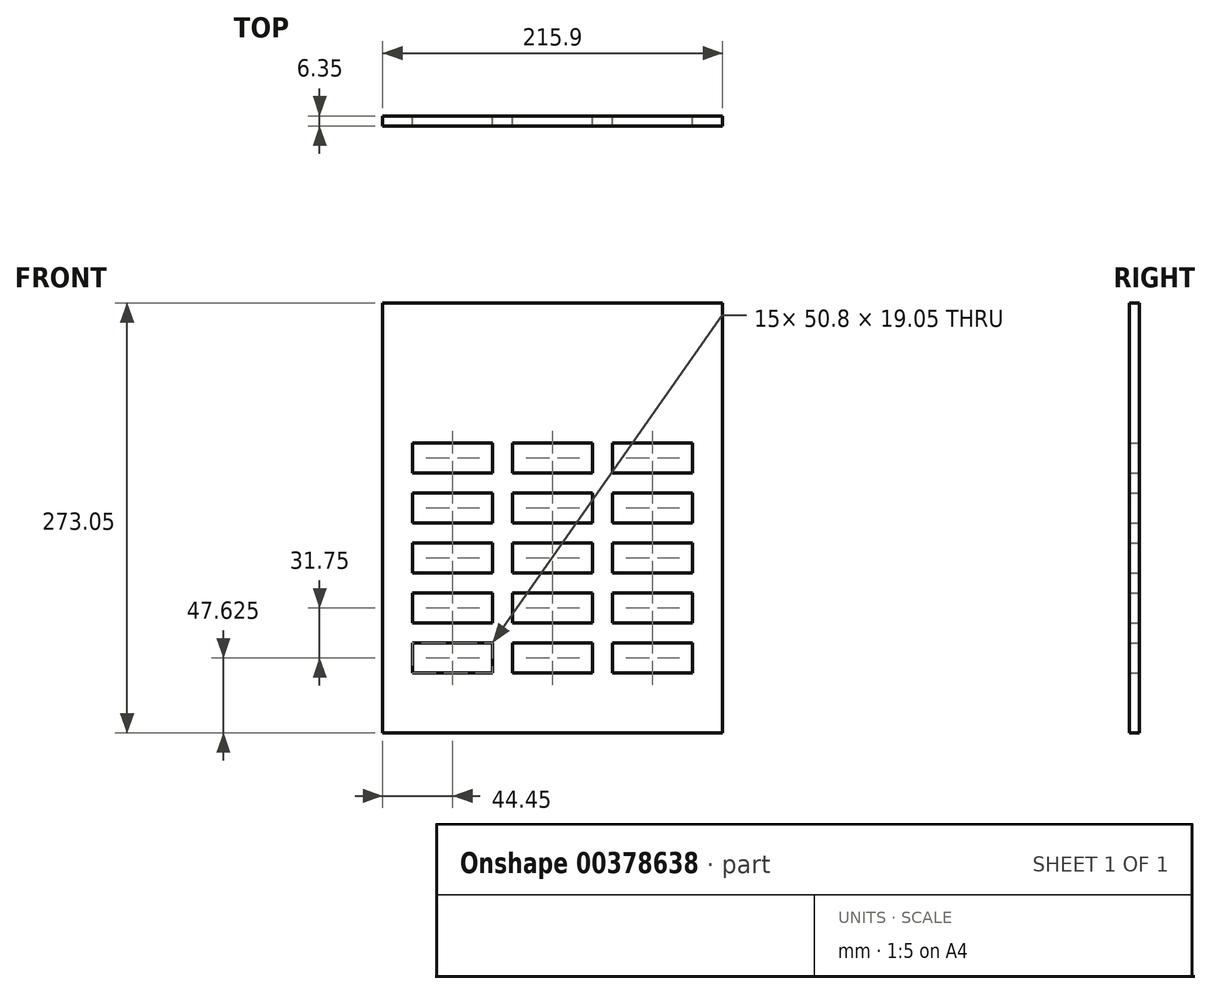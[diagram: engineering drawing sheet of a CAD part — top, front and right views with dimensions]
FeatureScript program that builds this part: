
annotation { "Feature Type Name" : "Feature", "Feature Type Description" : "" }
export const myFeature = defineFeature(function(context is Context, id is Id, definition is map)
    precondition{}
    {
        {
            var Q0;
            Q0=qCreatedBy(makeId("Front.planeOp"),FACE);
            var sketch = newSketch(context, id + "F0", { "sketchPlane" : qUnion([Q0])});
            skLineSegment(sketch, "E0.bottom", {"start": v(-107.95, 0) * mm, "end": v(107.95, 0) * mm});
            skLineSegment(sketch, "E0.top", {"start": v(-107.95, 273.05) * mm, "end": v(107.95, 273.05) * mm});
            skLineSegment(sketch, "E0.left", {"start": v(-107.95, 0) * mm, "end": v(-107.95, 273.05) * mm});
            skLineSegment(sketch, "E0.right", {"start": v(107.95, 0) * mm, "end": v(107.95, 273.05) * mm});
            skPoint(sketch, "E1", {"position": v(0, 273.05) * mm});
            skLineSegment(sketch, "E2.bottom", {"start": v(-88.9, 184.15) * mm, "end": v(-38.1, 184.15) * mm});
            skLineSegment(sketch, "E2.top", {"start": v(-88.9, 165.1) * mm, "end": v(-38.1, 165.1) * mm});
            skLineSegment(sketch, "E2.left", {"start": v(-88.9, 184.15) * mm, "end": v(-88.9, 165.1) * mm});
            skLineSegment(sketch, "E2.right", {"start": v(-38.1, 184.15) * mm, "end": v(-38.1, 165.1) * mm});
            skLineSegment(sketch, "E3.bottom", {"start": v(-25.4, 184.15) * mm, "end": v(25.4, 184.15) * mm});
            skLineSegment(sketch, "E3.top", {"start": v(-25.4, 165.1) * mm, "end": v(25.4, 165.1) * mm});
            skLineSegment(sketch, "E3.left", {"start": v(-25.4, 184.15) * mm, "end": v(-25.4, 165.1) * mm});
            skLineSegment(sketch, "E3.right", {"start": v(25.4, 184.15) * mm, "end": v(25.4, 165.1) * mm});
            skLineSegment(sketch, "E4.bottom", {"start": v(38.1, 184.15) * mm, "end": v(88.9, 184.15) * mm});
            skLineSegment(sketch, "E4.top", {"start": v(38.1, 165.1) * mm, "end": v(88.9, 165.1) * mm});
            skLineSegment(sketch, "E4.left", {"start": v(38.1, 184.15) * mm, "end": v(38.1, 165.1) * mm});
            skLineSegment(sketch, "E4.right", {"start": v(88.9, 184.15) * mm, "end": v(88.9, 165.1) * mm});
            skLineSegment(sketch, "E5.bottom", {"start": v(-88.9, 152.4) * mm, "end": v(-38.1, 152.4) * mm});
            skLineSegment(sketch, "E5.top", {"start": v(-88.9, 133.35) * mm, "end": v(-38.1, 133.35) * mm});
            skLineSegment(sketch, "E5.left", {"start": v(-88.9, 152.4) * mm, "end": v(-88.9, 133.35) * mm});
            skLineSegment(sketch, "E5.right", {"start": v(-38.1, 152.4) * mm, "end": v(-38.1, 133.35) * mm});
            skLineSegment(sketch, "E6.bottom", {"start": v(-25.4, 152.4) * mm, "end": v(25.4, 152.4) * mm});
            skLineSegment(sketch, "E6.top", {"start": v(-25.4, 133.35) * mm, "end": v(25.4, 133.35) * mm});
            skLineSegment(sketch, "E6.left", {"start": v(-25.4, 152.4) * mm, "end": v(-25.4, 133.35) * mm});
            skLineSegment(sketch, "E6.right", {"start": v(25.4, 152.4) * mm, "end": v(25.4, 133.35) * mm});
            skLineSegment(sketch, "E7.bottom", {"start": v(38.1, 152.4) * mm, "end": v(88.9, 152.4) * mm});
            skLineSegment(sketch, "E7.top", {"start": v(38.1, 133.35) * mm, "end": v(88.9, 133.35) * mm});
            skLineSegment(sketch, "E7.left", {"start": v(38.1, 152.4) * mm, "end": v(38.1, 133.35) * mm});
            skLineSegment(sketch, "E7.right", {"start": v(88.9, 152.4) * mm, "end": v(88.9, 133.35) * mm});
            skLineSegment(sketch, "E8.bottom", {"start": v(-88.9, 120.65) * mm, "end": v(-38.1, 120.65) * mm});
            skLineSegment(sketch, "E8.top", {"start": v(-88.9, 101.6) * mm, "end": v(-38.1, 101.6) * mm});
            skLineSegment(sketch, "E8.left", {"start": v(-88.9, 120.65) * mm, "end": v(-88.9, 101.6) * mm});
            skLineSegment(sketch, "E8.right", {"start": v(-38.1, 120.65) * mm, "end": v(-38.1, 101.6) * mm});
            skLineSegment(sketch, "E9.bottom", {"start": v(-25.4, 120.65) * mm, "end": v(25.4, 120.65) * mm});
            skLineSegment(sketch, "E9.top", {"start": v(-25.4, 101.6) * mm, "end": v(25.4, 101.6) * mm});
            skLineSegment(sketch, "E9.left", {"start": v(-25.4, 120.65) * mm, "end": v(-25.4, 101.6) * mm});
            skLineSegment(sketch, "E9.right", {"start": v(25.4, 120.65) * mm, "end": v(25.4, 101.6) * mm});
            skLineSegment(sketch, "E10.bottom", {"start": v(38.1, 120.65) * mm, "end": v(88.9, 120.65) * mm});
            skLineSegment(sketch, "E10.top", {"start": v(38.1, 101.6) * mm, "end": v(88.9, 101.6) * mm});
            skLineSegment(sketch, "E10.left", {"start": v(38.1, 120.65) * mm, "end": v(38.1, 101.6) * mm});
            skLineSegment(sketch, "E10.right", {"start": v(88.9, 120.65) * mm, "end": v(88.9, 101.6) * mm});
            skLineSegment(sketch, "E11.bottom", {"start": v(-88.9, 88.9) * mm, "end": v(-38.1, 88.9) * mm});
            skLineSegment(sketch, "E11.top", {"start": v(-88.9, 69.85) * mm, "end": v(-38.1, 69.85) * mm});
            skLineSegment(sketch, "E11.left", {"start": v(-88.9, 88.9) * mm, "end": v(-88.9, 69.85) * mm});
            skLineSegment(sketch, "E11.right", {"start": v(-38.1, 88.9) * mm, "end": v(-38.1, 69.85) * mm});
            skLineSegment(sketch, "E12.bottom", {"start": v(-25.4, 88.9) * mm, "end": v(25.4, 88.9) * mm});
            skLineSegment(sketch, "E12.top", {"start": v(-25.4, 69.85) * mm, "end": v(25.4, 69.85) * mm});
            skLineSegment(sketch, "E12.left", {"start": v(-25.4, 88.9) * mm, "end": v(-25.4, 69.85) * mm});
            skLineSegment(sketch, "E12.right", {"start": v(25.4, 88.9) * mm, "end": v(25.4, 69.85) * mm});
            skLineSegment(sketch, "E13.bottom", {"start": v(38.1, 88.9) * mm, "end": v(88.9, 88.9) * mm});
            skLineSegment(sketch, "E13.top", {"start": v(38.1, 69.85) * mm, "end": v(88.9, 69.85) * mm});
            skLineSegment(sketch, "E13.left", {"start": v(38.1, 88.9) * mm, "end": v(38.1, 69.85) * mm});
            skLineSegment(sketch, "E13.right", {"start": v(88.9, 88.9) * mm, "end": v(88.9, 69.85) * mm});
            skLineSegment(sketch, "E14.bottom", {"start": v(-88.9, 57.15) * mm, "end": v(-38.1, 57.15) * mm});
            skLineSegment(sketch, "E14.top", {"start": v(-88.9, 38.1) * mm, "end": v(-38.1, 38.1) * mm});
            skLineSegment(sketch, "E14.left", {"start": v(-88.9, 57.15) * mm, "end": v(-88.9, 38.1) * mm});
            skLineSegment(sketch, "E14.right", {"start": v(-38.1, 57.15) * mm, "end": v(-38.1, 38.1) * mm});
            skLineSegment(sketch, "E15.bottom", {"start": v(-25.4, 57.15) * mm, "end": v(25.4, 57.15) * mm});
            skLineSegment(sketch, "E15.top", {"start": v(-25.4, 38.1) * mm, "end": v(25.4, 38.1) * mm});
            skLineSegment(sketch, "E15.left", {"start": v(-25.4, 57.15) * mm, "end": v(-25.4, 38.1) * mm});
            skLineSegment(sketch, "E15.right", {"start": v(25.4, 57.15) * mm, "end": v(25.4, 38.1) * mm});
            skLineSegment(sketch, "E16.bottom", {"start": v(38.1, 57.15) * mm, "end": v(88.9, 57.15) * mm});
            skLineSegment(sketch, "E16.top", {"start": v(38.1, 38.1) * mm, "end": v(88.9, 38.1) * mm});
            skLineSegment(sketch, "E16.left", {"start": v(38.1, 57.15) * mm, "end": v(38.1, 38.1) * mm});
            skLineSegment(sketch, "E16.right", {"start": v(88.9, 57.15) * mm, "end": v(88.9, 38.1) * mm});
            skLineSegment(sketch, "E17", {"start": v(-88.9, 165.1) * mm, "end": v(-88.9, 152.4) * mm});
            skLineSegment(sketch, "E18", {"start": v(-88.9, 120.65) * mm, "end": v(-88.9, 133.35) * mm});
            skLineSegment(sketch, "E19", {"start": v(-88.9, 88.9) * mm, "end": v(-88.9, 101.6) * mm});
            skLineSegment(sketch, "E20", {"start": v(-88.9, 69.85) * mm, "end": v(-88.9, 57.15) * mm});
            skLineSegment(sketch, "E21", {"start": v(-38.1, 184.15) * mm, "end": v(-25.4, 184.15) * mm});
            skLineSegment(sketch, "E22", {"start": v(25.4, 184.15) * mm, "end": v(38.1, 184.15) * mm});
            skPoint(sketch, "E23", {"position": v(0, 184.15) * mm});
            skSolve(sketch);
        }
        {
            var Q0;
            Q0=makeQuery(id+"F0.imprint","IMPRINT",FACE,{"disambiguationData":[TD([[makeQuery(id+"F0.imprint","IMPRINT",EDGE,{"derivedFrom":sQuery(id+"F0.wireOp",EDGE,"E0.bottom")}),1.0]])]});
            extrude(context, id + "F1", {"entities" : qUnion([Q0]), "depth" : 6.35 * mm});
        }
    });
